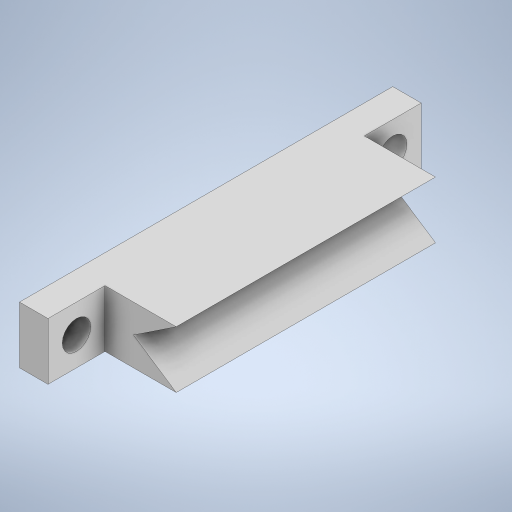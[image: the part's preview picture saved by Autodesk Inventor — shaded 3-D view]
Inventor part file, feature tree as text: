
AUTODESK INVENTOR PART (.ipt)
format: ipt  version: 2023 (Build 270158000, 158)  size: 269,312 bytes
history: native  units: mm
features: extrude x3, sketch x2
ambient origin geometry x8: Origin, YZ Plane, XZ Plane, XY Plane, X Axis, Y Axis, Z Axis, Center Point
bodies: Solid1 (feature_tree)
feature tree (5):
  sketch  "Sketch1"  dims[d0=10.0mm d1=0.0mm d2=5.0mm d3=0.0mm]
  extrude  "Extrusion1"  Depth=5.0mm TaperAngle=0.0deg
  extrude  "Extrusion2"  Depth=10.0mm TaperAngle=0.0deg
  extrude  "Extrusion4"  [1 undecoded]
  sketch  "Sketch2"  dims[d4=15.0mm d7=10.0mm d8=0.0mm]
note: 1 required parameter value undecoded (feature->parameter linkage not recoverable at this tier; creation-order binding heuristic only, values carry confidence <= 0.55)
